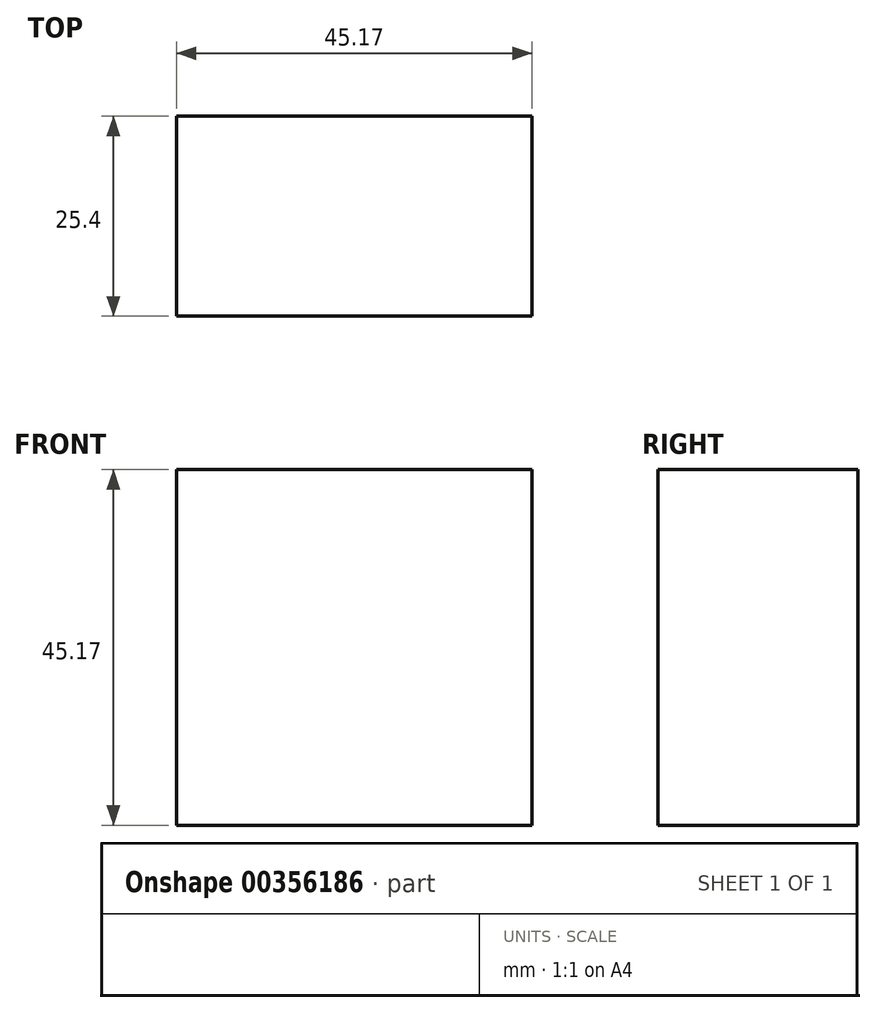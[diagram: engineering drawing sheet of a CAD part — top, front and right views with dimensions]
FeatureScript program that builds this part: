
annotation { "Feature Type Name" : "Feature", "Feature Type Description" : "" }
export const myFeature = defineFeature(function(context is Context, id is Id, definition is map)
    precondition{}
    {
        {
            var Q0;
            Q0=qCreatedBy(makeId("Front.planeOp"),FACE);
            var sketch = newSketch(context, id + "F0", { "sketchPlane" : qUnion([Q0])});
            skLineSegment(sketch, "E0.bottom", {"start": v(-11.47, 4.13) * mm, "end": v(-56.64, 4.13) * mm});
            skLineSegment(sketch, "E0.top", {"start": v(-11.47, 49.3) * mm, "end": v(-56.64, 49.3) * mm});
            skLineSegment(sketch, "E0.left", {"start": v(-11.47, 4.13) * mm, "end": v(-11.47, 49.3) * mm});
            skLineSegment(sketch, "E0.right", {"start": v(-56.64, 4.13) * mm, "end": v(-56.64, 49.3) * mm});
            skPoint(sketch, "E0.middle", {"position": v(-34.05, 26.72) * mm});
            skSolve(sketch);
        }
        {
            var Q0;
            Q0=makeQuery(id+"F0.imprint","IMPRINT",FACE,{"disambiguationData":[TD([[makeQuery(id+"F0.imprint","IMPRINT",EDGE,{"derivedFrom":sQuery(id+"F0.wireOp",EDGE,"E0.bottom")}),-1.0]])]});
            extrude(context, id + "F1", {"entities" : qUnion([Q0]), "depth" : 25.4 * mm});
        }
    });
